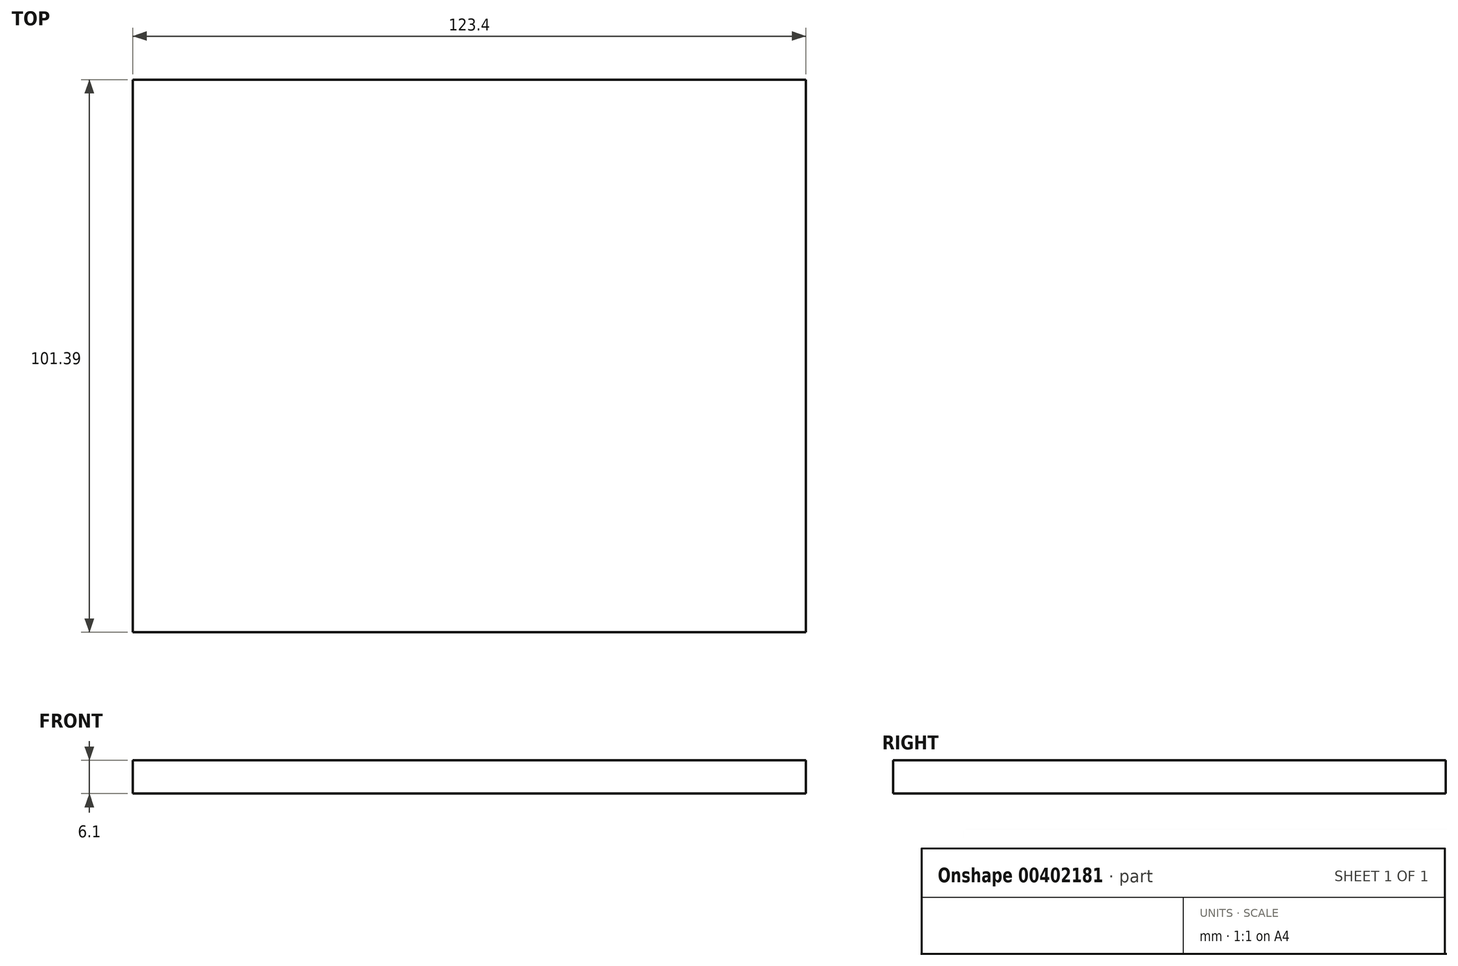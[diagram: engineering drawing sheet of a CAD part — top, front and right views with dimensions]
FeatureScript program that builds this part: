
annotation { "Feature Type Name" : "Feature", "Feature Type Description" : "" }
export const myFeature = defineFeature(function(context is Context, id is Id, definition is map)
    precondition{}
    {
        {
            var Q0;
            Q0=qCreatedBy(makeId("Top.planeOp"),FACE);
            var sketch = newSketch(context, id + "F0", { "sketchPlane" : qUnion([Q0])});
            skLineSegment(sketch, "E0.bottom", {"start": v(-61.22, 63.73) * mm, "end": v(60.9, 63.73) * mm});
            skLineSegment(sketch, "E0.top", {"start": v(-61.22, -62.66) * mm, "end": v(60.9, -62.66) * mm});
            skLineSegment(sketch, "E0.left", {"start": v(-61.22, 63.73) * mm, "end": v(-61.22, -62.66) * mm});
            skLineSegment(sketch, "E0.right", {"start": v(60.9, 63.73) * mm, "end": v(60.9, -62.66) * mm});
            skSolve(sketch);
        }
        {
            var Q0;
            Q0=makeQuery(id+"F0.imprint","IMPRINT",FACE,{"disambiguationData":[TD([[makeQuery(id+"F0.imprint","IMPRINT",EDGE,{"derivedFrom":sQuery(id+"F0.wireOp",EDGE,"E0.bottom")}),-1.0]])]});
            extrude(context, id + "F1", {"entities" : qUnion([Q0]), "depth" : 25.4 * mm});
        }
        {
            var Q0;
            Q0=makeQuery(id+"F1.opExtrude","SWEPT_FACE",FACE,{"disambiguationData":[OSD([sQuery(id+"F0.wireOp",EDGE,"E0.right")])]});
            extrude(context, id + "F2", {"entities" : qUnion([Q0]), "operationType" : NewBodyOperationType.ADD, "depth" : 25 * mm});
        }
        {
            var Q0;
            Q0=makeQuery(id+"F2.opExtrude","CAP_FACE",FACE,{"disambiguationData":[OSD([sQuery(id+"F0.wireOp",EDGE,"E0.right")])],"isStart":false});
            extrude(context, id + "F3", {"entities" : qUnion([Q0]), "operationType" : NewBodyOperationType.REMOVE, "oppositeDirection" : true, "depth" : 23.73 * mm});
        }
        {
            var Q0;
            {var subQ0=sQuery(id+"F0.wireOp",EDGE,"E0.bottom");Q0=makeQuery(id+"F2.boolean.opBoolean","MERGE",FACE,{"derivedFrom":[makeQuery(id+"F1.opExtrude","SWEPT_FACE",FACE,{"disambiguationData":[OSD([subQ0])]}),makeQuery(id+"F2.opExtrude","SWEPT_FACE",FACE,{"disambiguationData":[OSD([subQ0,sQuery(id+"F0.wireOp",EDGE,"E0.right")])]})]});}
            extrude(context, id + "F4", {"entities" : qUnion([Q0]), "operationType" : NewBodyOperationType.REMOVE, "oppositeDirection" : true, "depth" : 25 * mm});
        }
        {
            var Q0;
            {var subQ0=sQuery(id+"F0.wireOp",EDGE,"E0.right");Q0=makeQuery(id+"F2.boolean.opBoolean","MERGE",FACE,{"derivedFrom":[makeQuery(id+"F1.opExtrude","CAP_FACE",FACE,{"disambiguationData":[OSD([sQuery(id+"F0.wireOp",EDGE,"E0.bottom"),sQuery(id+"F0.wireOp",EDGE,"E0.top"),sQuery(id+"F0.wireOp",EDGE,"E0.left"),subQ0])],"isStart":true}),makeQuery(id+"F2.opExtrude","SWEPT_FACE",FACE,{"disambiguationData":[OSD([subQ0]),TDD([makeQuery(id+"F1.opExtrude","CAP_EDGE",EDGE,{"disambiguationData":[OSD([subQ0])],"isStart":true})])]})]});}
            extrude(context, id + "F5", {"entities" : qUnion([Q0]), "operationType" : NewBodyOperationType.REMOVE, "oppositeDirection" : true, "depth" : 19.3 * mm});
        }
    });
